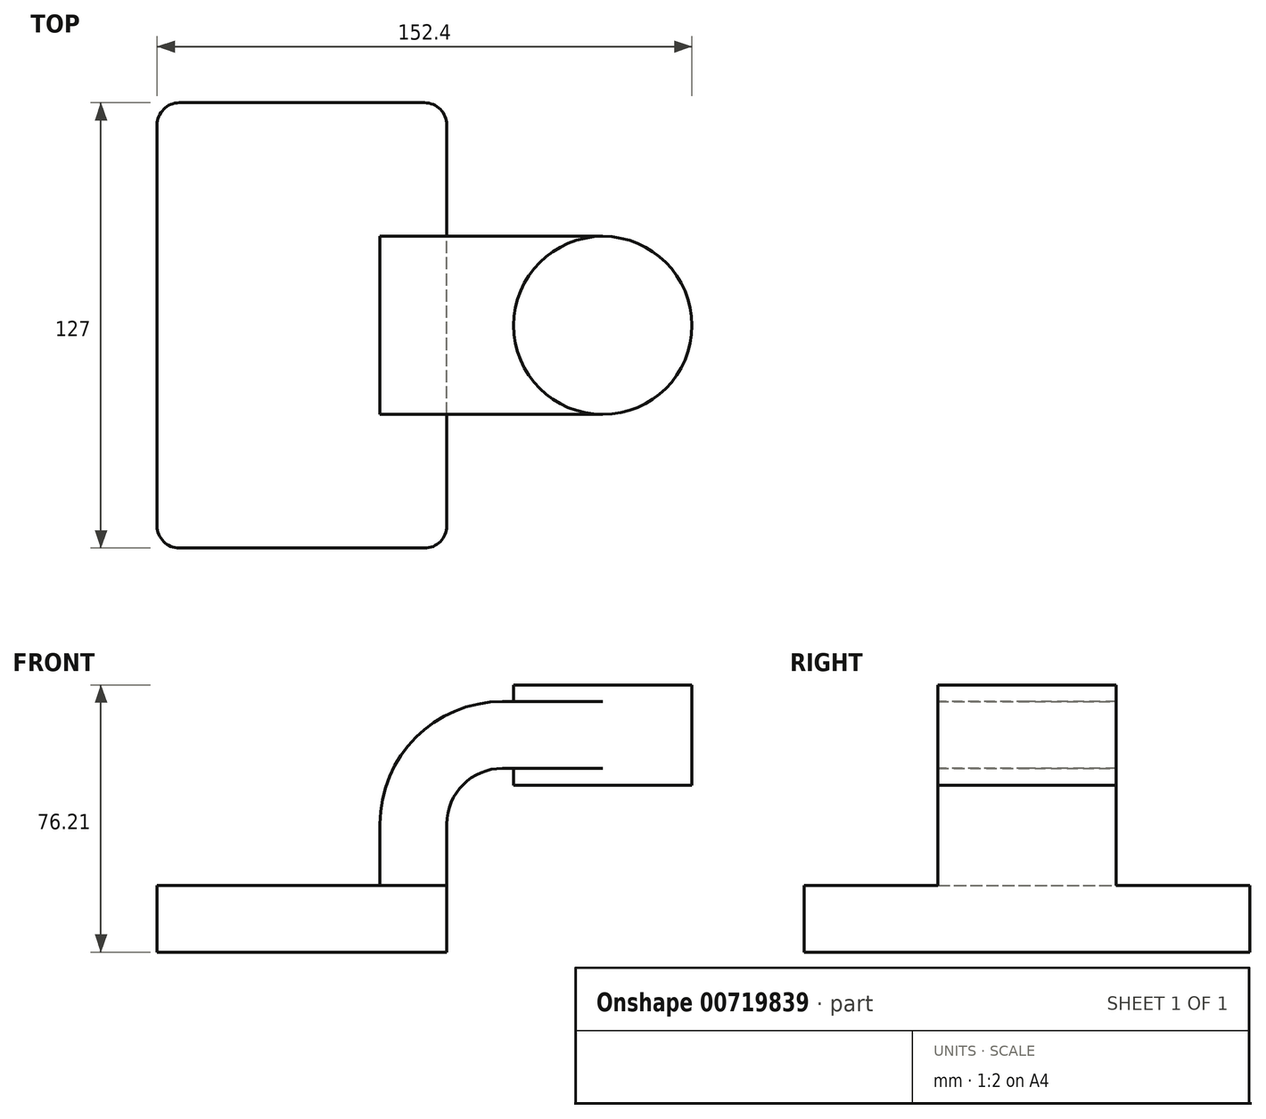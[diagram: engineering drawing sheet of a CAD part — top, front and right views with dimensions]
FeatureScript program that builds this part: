
annotation { "Feature Type Name" : "Feature", "Feature Type Description" : "" }
export const myFeature = defineFeature(function(context is Context, id is Id, definition is map)
    precondition{}
    {
        {
            var Q0;
            Q0=qCreatedBy(makeId("Front.planeOp"),FACE);
            var sketch = newSketch(context, id + "F0", { "sketchPlane" : qUnion([Q0])});
            skLineSegment(sketch, "E0.bottom", {"start": v(-41.28, -9.53) * mm, "end": v(41.28, -9.53) * mm});
            skLineSegment(sketch, "E0.top", {"start": v(-41.28, 9.53) * mm, "end": v(41.28, 9.53) * mm});
            skLineSegment(sketch, "E0.left", {"start": v(-41.28, -9.53) * mm, "end": v(-41.28, 9.53) * mm});
            skLineSegment(sketch, "E0.right", {"start": v(41.28, -9.53) * mm, "end": v(41.28, 9.53) * mm});
            skPoint(sketch, "E0.middle", {"position": v(0, 0) * mm});
            skLineSegment(sketch, "E1.bottom", {"start": v(60.33, 38.1) * mm, "end": v(111.12, 38.1) * mm});
            skLineSegment(sketch, "E1.top", {"start": v(60.33, 66.67) * mm, "end": v(111.12, 66.67) * mm});
            skLineSegment(sketch, "E1.left", {"start": v(60.33, 38.1) * mm, "end": v(60.33, 66.68) * mm});
            skLineSegment(sketch, "E1.right", {"start": v(111.12, 38.1) * mm, "end": v(111.12, 66.68) * mm});
            skPoint(sketch, "E1.middle", {"position": v(85.72, 52.39) * mm});
            skLineSegment(sketch, "E2", {"start": v(41.28, 9.53) * mm, "end": v(41.28, 27) * mm});
            skArc(sketch, "E3", {"start": v(41.27, 27) * mm, "mid": v(45.92, 38.23) * mm, "end": v(57.15, 42.88) * mm});
            skLineSegment(sketch, "E4", {"start": v(57.15, 42.88) * mm, "end": v(95.09, 42.88) * mm});
            skLineSegment(sketch, "E5.0", {"start": v(57.15, 61.93) * mm, "end": v(95.09, 61.93) * mm});
            skArc(sketch, "E5.1", {"start": v(22.23, 27) * mm, "mid": v(32.45, 51.7) * mm, "end": v(57.15, 61.93) * mm});
            skLineSegment(sketch, "E5.2", {"start": v(22.22, 9.53) * mm, "end": v(22.22, 27) * mm});
            skLineSegment(sketch, "E6", {"start": v(85.72, 38.1) * mm, "end": v(85.72, 66.67) * mm});
            skFitSpline(sketch, "E7", {"points": [v(-41.28, 9.53) * mm, v(57.15, 61.93) * mm], "startDerivative": vector(42.94, 108.88) * mm, "endDerivative": vector(109.03, -22.56) * mm});
            skSolve(sketch);
        }
        {
            var Q0;
            Q0=makeQuery(id+"F0.imprint","IMPRINT",FACE,{"disambiguationData":[TD([[makeQuery(id+"F0.imprint","IMPRINT",EDGE,{"derivedFrom":sQuery(id+"F0.wireOp",EDGE,"E0.bottom")}),1.0]])]});
            extrude(context, id + "F1", {"entities" : qUnion([Q0]), "endBound" : BoundingType.SYMMETRIC, "depth" : 127 * mm, "offsetDistance" : 25.4 * mm});
        }
        {
            var Q0;
            {var subQ1=sQuery(id+"F0.wireOp",EDGE,"E2");Q0=makeQuery(id+"F0.imprint","IMPRINT",FACE,{"disambiguationData":[TD([[makeQuery(id+"F0.imprint","IMPRINT",EDGE,{"derivedFrom":subQ1}),1.0]])]});}
            var Q1;
            {var subQ0=sQuery(id+"F0.wireOp",EDGE,"E4");var subQ1=sQuery(id+"F0.wireOp",EDGE,"E1.left");var subQ2=makeQuery(id+"F0.imprint","INTERSECT",VERTEX,{"derivedFrom":[subQ1,subQ0]});Q1=makeQuery(id+"F0.imprint","IMPRINT",FACE,{"disambiguationData":[TD([[makeQuery(id+"F0.imprint","IMPRINT",EDGE,{"disambiguationData":[TD([[subQ2,-1.0]])],"derivedFrom":subQ1}),-1.0]])]});}
            extrude(context, id + "F2", {"entities" : qUnion([Q0, Q1]), "operationType" : NewBodyOperationType.ADD, "endBound" : BoundingType.SYMMETRIC, "depth" : 50.8 * mm, "offsetDistance" : 25.4 * mm});
        }
        {
            var Q0;
            Q0=makeQuery(id+"F0.imprint","IMPRINT",FACE,{"disambiguationData":[TD([[makeQuery(id+"F0.imprint","IMPRINT",EDGE,{"derivedFrom":sQuery(id+"F0.wireOp",EDGE,"E5.1")}),1.0]])]});
            extrude(context, id + "F3", {"entities" : qUnion([Q0]), "operationType" : NewBodyOperationType.ADD, "endBound" : BoundingType.SYMMETRIC, "depth" : 15.88 * mm, "offsetDistance" : 25.4 * mm});
        }
        {
            var Q0;
            {var subQ0=sQuery(id+"F0.wireOp",EDGE,"E1.right");Q0=makeQuery(id+"F0.imprint","IMPRINT",FACE,{"disambiguationData":[TD([[makeQuery(id+"F0.imprint","IMPRINT",EDGE,{"derivedFrom":subQ0}),1.0]])]});}
            var Q1;
            Q1=sQuery(id+"F0.wireOp",EDGE,"E6");
            revolve(context, id + "F4", {"operationType" : NewBodyOperationType.ADD, "surfaceOperationType" : NewSurfaceOperationType.NEW, "entities" : qUnion([Q0]), "axis" : qUnion([Q1]), "revolveType" : RevolveType.FULL});
        }
        {
            var Q0;
            Q0=makeQuery(id+"F1.opExtrude","CAP_EDGE",EDGE,{"disambiguationData":[OSD([sQuery(id+"F0.wireOp",EDGE,"E0.left")])],"isStart":false});
            var Q1;
            Q1=makeQuery(id+"F1.opExtrude","CAP_EDGE",EDGE,{"disambiguationData":[OSD([sQuery(id+"F0.wireOp",EDGE,"E0.left")])],"isStart":true});
            var Q2;
            Q2=makeQuery(id+"F1.opExtrude","CAP_EDGE",EDGE,{"disambiguationData":[OSD([sQuery(id+"F0.wireOp",EDGE,"E0.right")])],"isStart":true});
            var Q3;
            Q3=makeQuery(id+"F1.opExtrude","CAP_EDGE",EDGE,{"disambiguationData":[OSD([sQuery(id+"F0.wireOp",EDGE,"E0.right")])],"isStart":false});
            fillet(context, id + "F5", {"entities" : qUnion([Q0, Q1, Q2, Q3]), "radius" : 6.35 * mm, "tangentPropagation" : true, "allowEdgeOverflow" : false});
        }
    });
